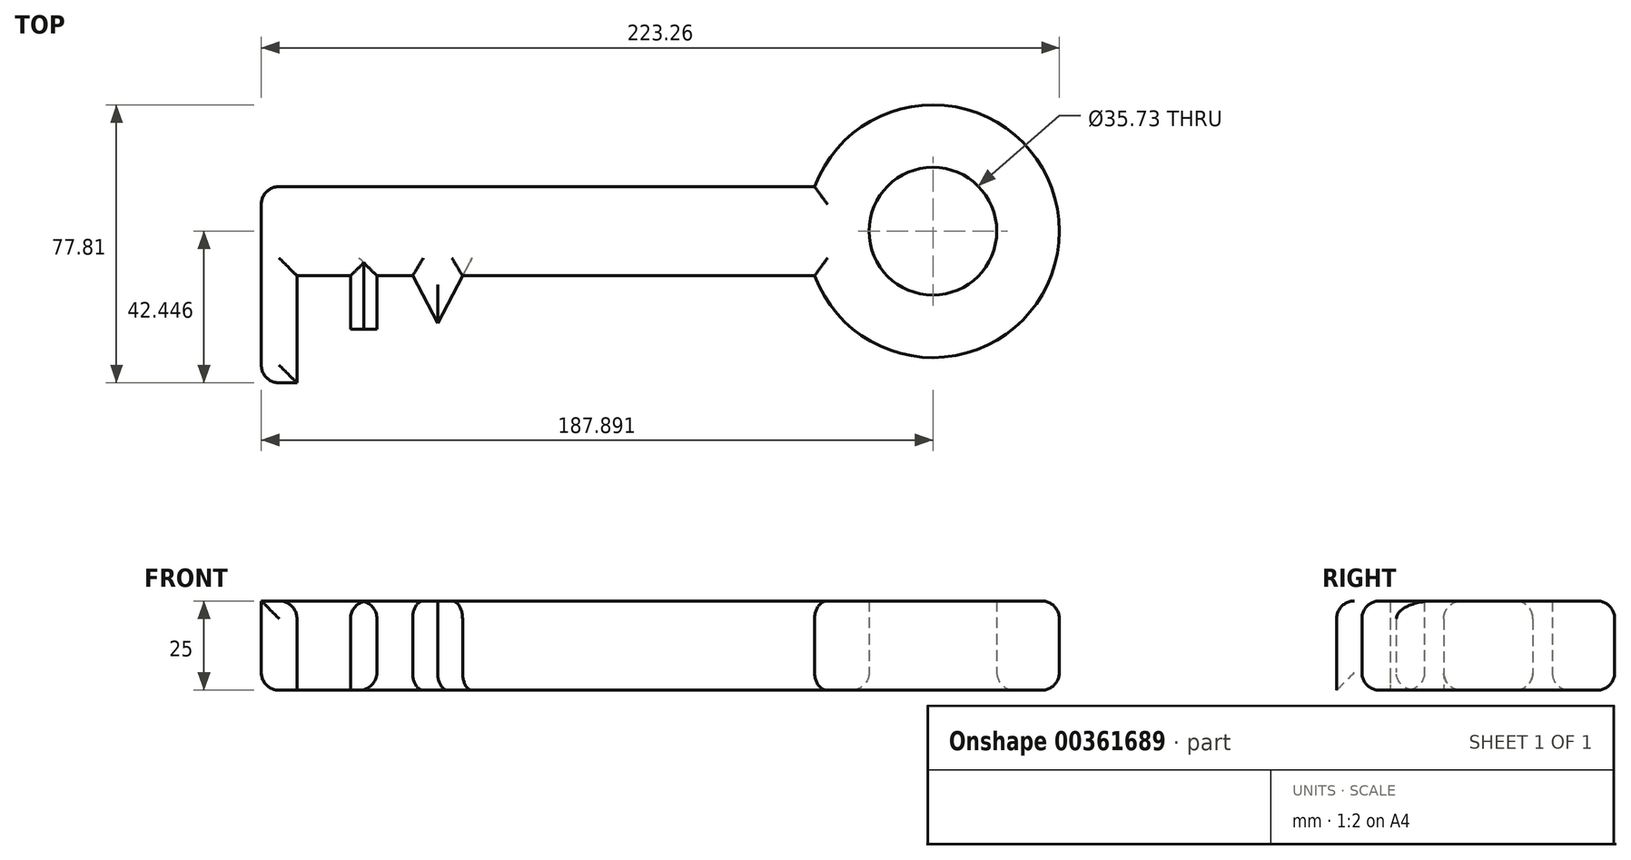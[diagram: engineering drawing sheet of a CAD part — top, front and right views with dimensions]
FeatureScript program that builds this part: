
annotation { "Feature Type Name" : "Feature", "Feature Type Description" : "" }
export const myFeature = defineFeature(function(context is Context, id is Id, definition is map)
    precondition{}
    {
        {
            var Q0;
            Q0=qCreatedBy(makeId("Top.planeOp"),FACE);
            var sketch = newSketch(context, id + "F0", { "sketchPlane" : qUnion([Q0])});
            skLineSegment(sketch, "E0.bottom", {"start": v(-19.72, 38.34) * mm, "end": v(-174.52, 38.34) * mm});
            skLineSegment(sketch, "E0.top", {"start": v(-19.72, 13.37) * mm, "end": v(-118.2, 13.37) * mm});
            skLineSegment(sketch, "E0.right", {"start": v(-174.52, 38.34) * mm, "end": v(-174.52, 13.37) * mm});
            skLineSegment(sketch, "E1.top", {"start": v(-174.52, -16.6) * mm, "end": v(-164.54, -16.6) * mm});
            skLineSegment(sketch, "E1.left", {"start": v(-174.52, 13.37) * mm, "end": v(-174.52, -16.6) * mm});
            skLineSegment(sketch, "E1.right", {"start": v(-164.54, 13.37) * mm, "end": v(-164.54, -16.6) * mm});
            skLineSegment(sketch, "E2.top", {"start": v(-149.55, -1.6) * mm, "end": v(-142.17, -1.6) * mm});
            skLineSegment(sketch, "E2.left", {"start": v(-149.55, 13.37) * mm, "end": v(-149.55, -1.6) * mm});
            skLineSegment(sketch, "E2.right", {"start": v(-142.17, 13.37) * mm, "end": v(-142.17, -1.6) * mm});
            skLineSegment(sketch, "E3", {"start": v(-132.19, 13.37) * mm, "end": v(-125.2, 0.12) * mm});
            skLineSegment(sketch, "E4", {"start": v(-125.2, 0.12) * mm, "end": v(-118.2, 13.37) * mm});
            skArc(sketch, "E5", {"start": v(-19.72, 13.37) * mm, "mid": v(48.74, 25.86) * mm, "end": v(-19.72, 38.34) * mm});
            skCircle(sketch, "E6", {"center": v(13.37, 25.86) * mm, "radius": 17.87 * mm});
            skLineSegment(sketch, "E7.trimOffspring", {"start": v(-149.55, 13.37) * mm, "end": v(-164.54, 13.37) * mm});
            skLineSegment(sketch, "E8.trimOffspring", {"start": v(-132.19, 13.37) * mm, "end": v(-142.17, 13.37) * mm});
            skSolve(sketch);
        }
        {
            var Q0;
            Q0 = qSketchRegion(id + "F0", true);
            extrude(context, id + "F1", {"entities" : qUnion([Q0]), "depth" : 25 * mm});
        }
        {
            var Q0;
            Q0=makeQuery(id+"F1.opExtrude","CAP_EDGE",EDGE,{"disambiguationData":[OSD([sQuery(id+"F0.wireOp",EDGE,"E0.top")])],"isStart":false});
            var Q1;
            Q1=makeQuery(id+"F1.opExtrude","CAP_EDGE",EDGE,{"disambiguationData":[OSD([sQuery(id+"F0.wireOp",EDGE,"E4")])],"isStart":false});
            var Q2;
            Q2=makeQuery(id+"F1.opExtrude","CAP_EDGE",EDGE,{"disambiguationData":[OSD([sQuery(id+"F0.wireOp",EDGE,"E8.trimOffspring")])],"isStart":false});
            var Q3;
            Q3=makeQuery(id+"F1.opExtrude","CAP_EDGE",EDGE,{"disambiguationData":[OSD([sQuery(id+"F0.wireOp",EDGE,"E7.trimOffspring")])],"isStart":false});
            var Q4;
            Q4=makeQuery(id+"F1.opExtrude","CAP_EDGE",EDGE,{"disambiguationData":[OSD([sQuery(id+"F0.wireOp",EDGE,"E1.right")])],"isStart":false});
            var Q5;
            Q5=makeQuery(id+"F1.opExtrude","CAP_EDGE",EDGE,{"disambiguationData":[OSD([sQuery(id+"F0.wireOp",EDGE,"E2.left")])],"isStart":false});
            var Q6;
            Q6=makeQuery(id+"F1.opExtrude","CAP_EDGE",EDGE,{"disambiguationData":[OSD([sQuery(id+"F0.wireOp",EDGE,"E2.right")])],"isStart":false});
            var Q7;
            Q7=makeQuery(id+"F1.opExtrude","CAP_EDGE",EDGE,{"disambiguationData":[OSD([sQuery(id+"F0.wireOp",EDGE,"E3")])],"isStart":false});
            var Q8;
            Q8=makeQuery(id+"F1.opExtrude","CAP_EDGE",EDGE,{"disambiguationData":[OSD([sQuery(id+"F0.wireOp",EDGE,"E5")])],"isStart":false});
            var Q9;
            Q9=makeQuery(id+"F1.opExtrude","CAP_EDGE",EDGE,{"disambiguationData":[OSD([sQuery(id+"F0.wireOp",EDGE,"E1.top")])],"isStart":false});
            var Q10;
            Q10=makeQuery(id+"F1.opExtrude","CAP_EDGE",EDGE,{"disambiguationData":[OSD([sQuery(id+"F0.wireOp",EDGE,"E0.bottom")])],"isStart":false});
            var Q11;
            Q11=makeQuery(id+"F1.opExtrude","SWEPT_EDGE",EDGE,{"disambiguationData":[OSD([sQuery(id+"F0.wireOp",EDGE,"E0.bottom"),sQuery(id+"F0.wireOp",EDGE,"E0.right")])]});
            var Q12;
            Q12=makeQuery(id+"F1.opExtrude","SWEPT_EDGE",EDGE,{"disambiguationData":[OSD([sQuery(id+"F0.wireOp",EDGE,"E1.top"),sQuery(id+"F0.wireOp",EDGE,"E1.left")])]});
            var Q13;
            Q13=makeQuery(id+"F1.opExtrude","CAP_EDGE",EDGE,{"disambiguationData":[OSD([sQuery(id+"F0.wireOp",EDGE,"E0.right"),sQuery(id+"F0.wireOp",EDGE,"E1.left")])],"isStart":true});
            var Q14;
            Q14=makeQuery(id+"F1.opExtrude","CAP_EDGE",EDGE,{"disambiguationData":[OSD([sQuery(id+"F0.wireOp",EDGE,"E0.bottom")])],"isStart":true});
            var Q15;
            Q15=makeQuery(id+"F1.opExtrude","CAP_EDGE",EDGE,{"disambiguationData":[OSD([sQuery(id+"F0.wireOp",EDGE,"E0.top")])],"isStart":true});
            var Q16;
            Q16=makeQuery(id+"F1.opExtrude","CAP_EDGE",EDGE,{"disambiguationData":[OSD([sQuery(id+"F0.wireOp",EDGE,"E5")])],"isStart":true});
            var Q17;
            Q17=makeQuery(id+"F1.opExtrude","CAP_EDGE",EDGE,{"disambiguationData":[OSD([sQuery(id+"F0.wireOp",EDGE,"E6")])],"isStart":true});
            var Q18;
            Q18=makeQuery(id+"F1.opExtrude","CAP_EDGE",EDGE,{"disambiguationData":[OSD([sQuery(id+"F0.wireOp",EDGE,"E8.trimOffspring")])],"isStart":true});
            var Q19;
            Q19=makeQuery(id+"F1.opExtrude","CAP_EDGE",EDGE,{"disambiguationData":[OSD([sQuery(id+"F0.wireOp",EDGE,"E3")])],"isStart":true});
            var Q20;
            Q20=makeQuery(id+"F1.opExtrude","CAP_EDGE",EDGE,{"disambiguationData":[OSD([sQuery(id+"F0.wireOp",EDGE,"E2.right")])],"isStart":true});
            fillet(context, id + "F2", {"entities" : qUnion([Q0, Q1, Q2, Q3, Q4, Q5, Q6, Q7, Q8, Q9, Q10, Q11, Q12, Q13, Q14, Q15, Q16, Q17, Q18, Q19, Q20]), "radius" : 5 * mm, "tangentPropagation" : true, "allowEdgeOverflow" : false});
        }
    });
